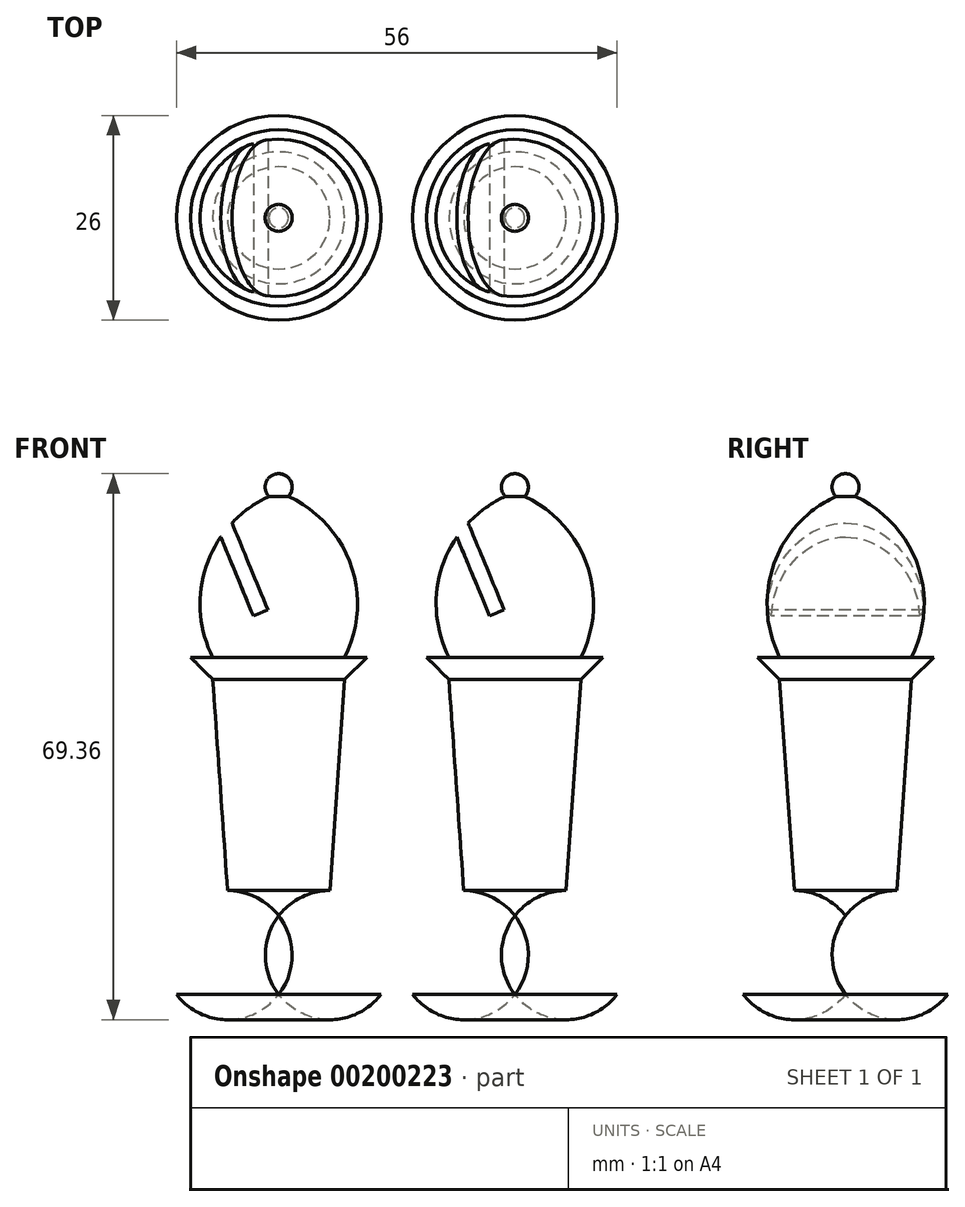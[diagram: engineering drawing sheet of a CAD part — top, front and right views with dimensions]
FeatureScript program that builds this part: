
annotation { "Feature Type Name" : "Feature", "Feature Type Description" : "" }
export const myFeature = defineFeature(function(context is Context, id is Id, definition is map)
    precondition{}
    {
        {
            var Q0;
            Q0=qCreatedBy(makeId("Front.planeOp"),FACE);
            var sketch = newSketch(context, id + "F0", { "sketchPlane" : qUnion([Q0])});
            skLineSegment(sketch, "E0", {"start": v(0, 0) * mm, "end": v(-13, 0) * mm});
            skArc(sketch, "E1", {"start": v(-13, 0) * mm, "mid": v(-13.86, 8.62) * mm, "end": v(-6.5, 13.2) * mm});
            skPoint(sketch, "E1.centerSnap0", {"position": v(-6.5, 0) * mm});
            skLineSegment(sketch, "E2", {"start": v(0, 0) * mm, "end": v(0, 66.26) * mm});
            skLineSegment(sketch, "E3", {"start": v(-6.5, 13.2) * mm, "end": v(-8.37, 40) * mm});
            skLineSegment(sketch, "E4", {"start": v(-8.37, 40) * mm, "end": v(-11.2, 42.83) * mm});
            skLineSegment(sketch, "E5", {"start": v(-11.2, 42.83) * mm, "end": v(-8.37, 42.83) * mm});
            skArc(sketch, "E6", {"start": v(-8.37, 42.83) * mm, "mid": v(-9.16, 54.56) * mm, "end": v(-1.24, 63.26) * mm});
            skPoint(sketch, "E7.orphan", {"position": v(0, 63.76) * mm});
            skPoint(sketch, "E8.MirrorCS.start.orphan", {"position": v(8.37, 42.83) * mm});
            skPoint(sketch, "E9.MirrorCS.start.orphan", {"position": v(11.2, 42.83) * mm});
            skPoint(sketch, "E10.MirrorCS.start.orphan", {"position": v(8.37, 40) * mm});
            skPoint(sketch, "E11.MirrorCS.start.orphan", {"position": v(6.5, 13.2) * mm});
            skPoint(sketch, "E12.MirrorCS.start.orphan", {"position": v(13, 0) * mm});
            skPoint(sketch, "E13.orphan", {"position": v(0, 70) * mm});
            skArc(sketch, "E14", {"start": v(0, 66.16) * mm, "mid": v(-1.58, 65.12) * mm, "end": v(-1.24, 63.26) * mm});
            skSolve(sketch);
        }
        {
            var Q0;
            Q0=makeQuery(id+"F0.imprint","IMPRINT",FACE,{"disambiguationData":[TD([[makeQuery(id+"F0.imprint","IMPRINT",EDGE,{"derivedFrom":sQuery(id+"F0.wireOp",EDGE,"E0")}),-1.0]])]});
            var Q1;
            Q1=sQuery(id+"F0.wireOp",EDGE,"E2");
            revolve(context, id + "F1", {"entities" : qUnion([Q0]), "axis" : qUnion([Q1]), "revolveType" : RevolveType.FULL});
        }
        {
            var Q0;
            Q0=qCreatedBy(makeId("Front.planeOp"),FACE);
            var sketch = newSketch(context, id + "F2", { "sketchPlane" : qUnion([Q0])});
            skLineSegment(sketch, "E15", {"start": v(-35.1, 56.54) * mm, "end": v(1.85, 71.85) * mm});
            skSolve(sketch);
        }
        {
            var Q0;
            Q0=sQuery(id+"F2.wireOp",EDGE,"E15");
            var Q1;
            Q1=qCreatedBy(makeId("Right.planeOp"),FACE);
            cPlane(context, id + "F3", {"entities" : qUnion([Q0, Q1]), "cplaneType" : CPlaneType.LINE_ANGLE, "offset" : 25 * mm, "angle" : 0 * degree, "width" : 150 * mm, "height" : 150 * mm});
        }
        {
            var Q0;
            Q0=qCreatedBy(id+"F3.planeOp",FACE);
            var sketch = newSketch(context, id + "F4", { "sketchPlane" : qUnion([Q0])});
            skLineSegment(sketch, "E16", {"start": v(15.44, 21.43) * mm, "end": v(15.44, -23.04) * mm});
            skLineSegment(sketch, "E17", {"start": v(15.44, 21.43) * mm, "end": v(17.44, 21.43) * mm});
            skLineSegment(sketch, "E18", {"start": v(17.44, 21.43) * mm, "end": v(17.44, -23.04) * mm});
            skLineSegment(sketch, "E19", {"start": v(17.44, -23.04) * mm, "end": v(15.44, -23.04) * mm});
            skSolve(sketch);
        }
        {
            var Q0;
            Q0=makeQuery(id+"F4.imprint","IMPRINT",FACE,{"disambiguationData":[TD([[makeQuery(id+"F4.imprint","IMPRINT",EDGE,{"derivedFrom":sQuery(id+"F4.wireOp",EDGE,"E16")}),1.0]])]});
            extrude(context, id + "F5", {"entities" : qUnion([Q0]), "operationType" : NewBodyOperationType.REMOVE, "oppositeDirection" : true, "depth" : 20 * mm});
        }
        {
            var Q0;
            Q0=makeQuery(id+"F1.opRevolve","SWEPT_BODY",BODY,{"disambiguationData":[OSD([sQuery(id+"F0.wireOp",EDGE,"E0"),sQuery(id+"F0.wireOp",EDGE,"E1"),sQuery(id+"F0.wireOp",EDGE,"E2"),sQuery(id+"F0.wireOp",EDGE,"E3"),sQuery(id+"F0.wireOp",EDGE,"E4"),sQuery(id+"F0.wireOp",EDGE,"E5"),sQuery(id+"F0.wireOp",EDGE,"E6"),sQuery(id+"F0.wireOp",EDGE,"E14")])]});
            transform(context, id + "F6", {"entities" : qUnion([Q0]), "transformType" : TransformType.TRANSLATION_3D, "dx" : 30 * mm, "dy" : 0 * mm, "dz" : 0 * mm, "makeCopy" : true});
        }
    });
